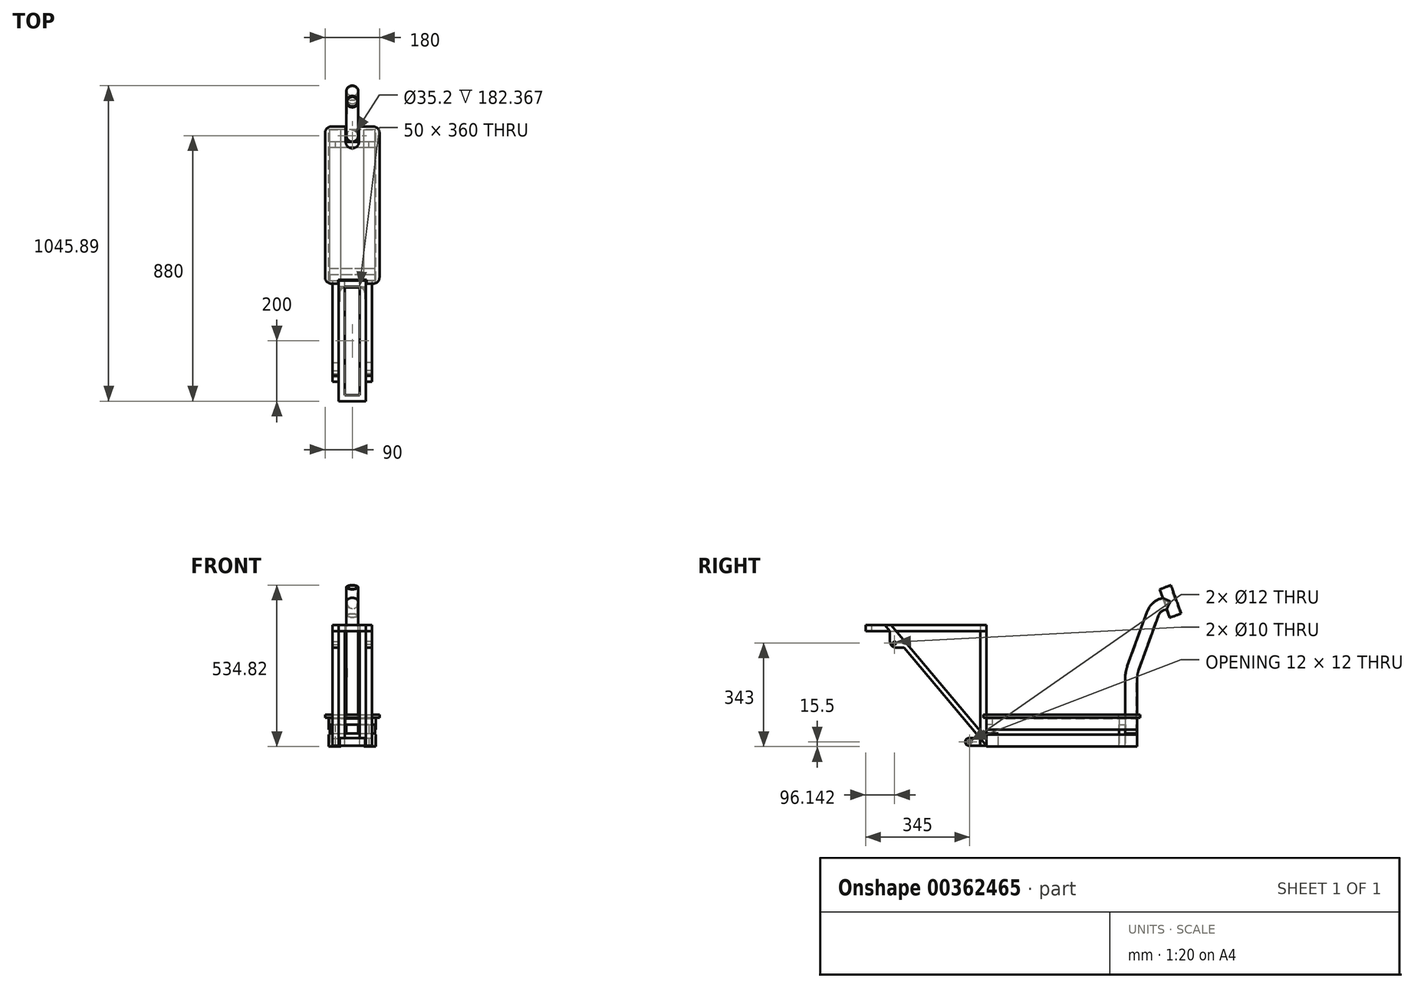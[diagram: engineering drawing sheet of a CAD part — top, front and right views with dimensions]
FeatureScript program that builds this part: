
annotation { "Feature Type Name" : "Feature", "Feature Type Description" : "" }
export const myFeature = defineFeature(function(context is Context, id is Id, definition is map)
    precondition{}
    {
        {
            var Q0;
            Q0=qCreatedBy(makeId("Front.planeOp"),FACE);
            var sketch = newSketch(context, id + "F0", { "sketchPlane" : qUnion([Q0])});
            skLineSegment(sketch, "E0.bottom", {"start": v(75, 45) * mm, "end": v(-75, 45) * mm, "construction": true});
            skLineSegment(sketch, "E0.top", {"start": v(75, -45) * mm, "end": v(-75, -45) * mm, "construction": true});
            skLineSegment(sketch, "E0.left", {"start": v(75, 45) * mm, "end": v(75, -45) * mm, "construction": true});
            skLineSegment(sketch, "E0.right", {"start": v(-75, 45) * mm, "end": v(-75, -45) * mm, "construction": true});
            skPoint(sketch, "E0.middle", {"position": v(0, 0) * mm});
            skLineSegment(sketch, "E1", {"start": v(-75, 45) * mm, "end": v(-75, 8) * mm});
            skLineSegment(sketch, "E2", {"start": v(-75, 8) * mm, "end": v(-78, 8) * mm});
            skLineSegment(sketch, "E3", {"start": v(-78, 8) * mm, "end": v(-78, 48) * mm});
            skLineSegment(sketch, "E4", {"start": v(-78, 48) * mm, "end": v(-38, 48) * mm});
            skLineSegment(sketch, "E5", {"start": v(-38, 48) * mm, "end": v(-38, 45) * mm});
            skLineSegment(sketch, "E6", {"start": v(-38, 45) * mm, "end": v(-75, 45) * mm});
            skLineSegment(sketch, "E7.MirrorCS", {"start": v(78, 48) * mm, "end": v(38, 48) * mm});
            skLineSegment(sketch, "E8.MirrorCS", {"start": v(38, 45) * mm, "end": v(75, 45) * mm});
            skLineSegment(sketch, "E9.MirrorCS", {"start": v(78, 8) * mm, "end": v(78, 48) * mm});
            skLineSegment(sketch, "E10.MirrorCS", {"start": v(75, 45) * mm, "end": v(75, 8) * mm});
            skLineSegment(sketch, "E11.MirrorCS", {"start": v(75, 8) * mm, "end": v(78, 8) * mm});
            skLineSegment(sketch, "E12.MirrorCS", {"start": v(38, 48) * mm, "end": v(38, 45) * mm});
            skLineSegment(sketch, "E13.MirrorCS", {"start": v(38, -48) * mm, "end": v(38, -45) * mm});
            skLineSegment(sketch, "E14.MirrorCS", {"start": v(75, -8) * mm, "end": v(78, -8) * mm});
            skLineSegment(sketch, "E15.MirrorCS", {"start": v(-38, -48) * mm, "end": v(-38, -45) * mm});
            skLineSegment(sketch, "E16.MirrorCS", {"start": v(-75, -8) * mm, "end": v(-78, -8) * mm});
            skLineSegment(sketch, "E17.MirrorCS", {"start": v(75, -45) * mm, "end": v(75, -8) * mm});
            skLineSegment(sketch, "E18.MirrorCS", {"start": v(78, -8) * mm, "end": v(78, -48) * mm});
            skLineSegment(sketch, "E19.MirrorCS", {"start": v(38, -45) * mm, "end": v(75, -45) * mm});
            skLineSegment(sketch, "E20.MirrorCS", {"start": v(78, -48) * mm, "end": v(38, -48) * mm});
            skLineSegment(sketch, "E21.MirrorCS", {"start": v(-38, -45) * mm, "end": v(-75, -45) * mm});
            skLineSegment(sketch, "E22.MirrorCS", {"start": v(-78, -8) * mm, "end": v(-78, -48) * mm});
            skLineSegment(sketch, "E23.MirrorCS", {"start": v(-75, -45) * mm, "end": v(-75, -8) * mm});
            skLineSegment(sketch, "E24.MirrorCS", {"start": v(-78, -48) * mm, "end": v(-38, -48) * mm});
            skLineSegment(sketch, "E25.MirrorCS", {"start": v(75, -45) * mm, "end": v(75, 45) * mm, "construction": true});
            skLineSegment(sketch, "E26.MirrorCS", {"start": v(-75, -45) * mm, "end": v(-75, 45) * mm, "construction": true});
            skSolve(sketch);
        }
        {
            var Q0;
            Q0=makeQuery(id+"F0.imprint","IMPRINT",FACE,{"disambiguationData":[TD([[makeQuery(id+"F0.imprint","IMPRINT",EDGE,{"derivedFrom":sQuery(id+"F0.wireOp",EDGE,"E1")}),-1.0]])]});
            var Q1;
            Q1=makeQuery(id+"F0.imprint","IMPRINT",FACE,{"disambiguationData":[TD([[makeQuery(id+"F0.imprint","IMPRINT",EDGE,{"derivedFrom":sQuery(id+"F0.wireOp",EDGE,"E7.MirrorCS")}),1.0]])]});
            extrude(context, id + "F1", {"entities" : qUnion([Q0, Q1]), "depth" : 500 * mm, "offsetDistance" : 25 * mm});
        }
        {
            var Q0;
            Q0=makeQuery(id+"F0.imprint","IMPRINT",FACE,{"disambiguationData":[TD([[makeQuery(id+"F0.imprint","IMPRINT",EDGE,{"derivedFrom":sQuery(id+"F0.wireOp",EDGE,"E15.MirrorCS")}),1.0]])]});
            var Q1;
            Q1=makeQuery(id+"F0.imprint","IMPRINT",FACE,{"disambiguationData":[TD([[makeQuery(id+"F0.imprint","IMPRINT",EDGE,{"derivedFrom":sQuery(id+"F0.wireOp",EDGE,"E13.MirrorCS")}),-1.0]])]});
            extrude(context, id + "F2", {"entities" : qUnion([Q0, Q1]), "depth" : 500 * mm, "offsetDistance" : 25 * mm});
        }
        {
            var Q0;
            Q0=qCreatedBy(makeId("Front.planeOp"),FACE);
            var sketch = newSketch(context, id + "F3", { "sketchPlane" : qUnion([Q0])});
            skLineSegment(sketch, "E27.top", {"start": v(75, -45) * mm, "end": v(-75, -45) * mm});
            skLineSegment(sketch, "E27.left", {"start": v(75, -5) * mm, "end": v(75, -45) * mm});
            skLineSegment(sketch, "E27.right", {"start": v(-75, -5) * mm, "end": v(-75, -45) * mm});
            skLineSegment(sketch, "E28", {"start": v(75, -5) * mm, "end": v(-75, -5) * mm});
            skSolve(sketch);
        }
        {
            var Q0;
            Q0 = qSketchRegion(id + "F3", true);
            extrude(context, id + "F4", {"entities" : qUnion([Q0]), "depth" : 40 * mm, "offsetDistance" : 25 * mm});
        }
        {
            var Q0;
            Q0=makeQuery(id+"F4.opExtrude","CAP_FACE",FACE,{"disambiguationData":[OSD([sQuery(id+"F3.wireOp",EDGE,"E27.top"),sQuery(id+"F3.wireOp",EDGE,"E27.left"),sQuery(id+"F3.wireOp",EDGE,"E27.right"),sQuery(id+"F3.wireOp",EDGE,"E28")])],"isStart":false});
            var sketch = newSketch(context, id + "F5", { "sketchPlane" : qUnion([Q0])});
            skLineSegment(sketch, "E29.0", {"start": v(75, 45) * mm, "end": v(-75, 45) * mm});
            skLineSegment(sketch, "E29.1", {"start": v(75, 45) * mm, "end": v(75, -45) * mm});
            skLineSegment(sketch, "E29.2", {"start": v(-75, -45) * mm, "end": v(-75, 45) * mm});
            skLineSegment(sketch, "E30.0", {"start": v(55, 25) * mm, "end": v(55, -45) * mm});
            skLineSegment(sketch, "E30.1", {"start": v(55, 25) * mm, "end": v(-55, 25) * mm});
            skLineSegment(sketch, "E30.2", {"start": v(-55, -45) * mm, "end": v(-55, 25) * mm});
            skLineSegment(sketch, "E31", {"start": v(75, -45) * mm, "end": v(55, -45) * mm});
            skLineSegment(sketch, "E32", {"start": v(-55, -45) * mm, "end": v(-75, -45) * mm});
            skSolve(sketch);
        }
        {
            var Q0;
            Q0 = qSketchRegion(id + "F5", true);
            extrude(context, id + "F6", {"entities" : qUnion([Q0]), "depth" : 20 * mm, "offsetDistance" : 25 * mm});
        }
        {
            var Q0;
            Q0=qCreatedBy(makeId("Front.planeOp"),FACE);
            cPlane(context, id + "F7", {"entities" : qUnion([Q0]), "cplaneType" : CPlaneType.OFFSET, "offset" : 500 * mm, "width" : 150 * mm, "height" : 150 * mm});
        }
        {
            var Q0;
            Q0=qCreatedBy(id+"F7.planeOp",FACE);
            var sketch = newSketch(context, id + "F8", { "sketchPlane" : qUnion([Q0])});
            skLineSegment(sketch, "E33.bottom", {"start": v(-75, -45) * mm, "end": v(75, -45) * mm});
            skLineSegment(sketch, "E33.top", {"start": v(-75, -5) * mm, "end": v(75, -5) * mm});
            skLineSegment(sketch, "E33.left", {"start": v(-75, -45) * mm, "end": v(-75, -5) * mm});
            skLineSegment(sketch, "E33.right", {"start": v(75, -45) * mm, "end": v(75, -5) * mm});
            skLineSegment(sketch, "E34.bottom", {"start": v(-75, 45) * mm, "end": v(75, 45) * mm});
            skLineSegment(sketch, "E34.top", {"start": v(-75, 25) * mm, "end": v(75, 25) * mm});
            skLineSegment(sketch, "E34.left", {"start": v(-75, 45) * mm, "end": v(-75, 25) * mm});
            skLineSegment(sketch, "E34.right", {"start": v(75, 45) * mm, "end": v(75, 25) * mm});
            skSolve(sketch);
        }
        {
            var Q0;
            Q0=makeQuery(id+"F8.imprint","IMPRINT",FACE,{"disambiguationData":[TD([[makeQuery(id+"F8.imprint","IMPRINT",EDGE,{"derivedFrom":sQuery(id+"F8.wireOp",EDGE,"E34.bottom")}),-1.0]])]});
            extrude(context, id + "F9", {"entities" : qUnion([Q0]), "oppositeDirection" : true, "depth" : 20 * mm, "offsetDistance" : 25 * mm});
        }
        {
            var Q0;
            Q0=makeQuery(id+"F8.imprint","IMPRINT",FACE,{"disambiguationData":[TD([[makeQuery(id+"F8.imprint","IMPRINT",EDGE,{"derivedFrom":sQuery(id+"F8.wireOp",EDGE,"E33.bottom")}),1.0]])]});
            extrude(context, id + "F10", {"entities" : qUnion([Q0]), "oppositeDirection" : true, "depth" : 40 * mm, "offsetDistance" : 25 * mm});
        }
        {
            var Q0;
            Q0=qCreatedBy(id+"F7.planeOp",FACE);
            var sketch = newSketch(context, id + "F11", { "sketchPlane" : qUnion([Q0])});
            skLineSegment(sketch, "E35.bottom", {"start": v(-25, -45) * mm, "end": v(-45, -45) * mm});
            skLineSegment(sketch, "E35.top", {"start": v(-25, 335) * mm, "end": v(-45, 335) * mm});
            skLineSegment(sketch, "E35.left", {"start": v(-25, -45) * mm, "end": v(-25, 335) * mm});
            skLineSegment(sketch, "E35.right", {"start": v(-45, -45) * mm, "end": v(-45, 335) * mm});
            skLineSegment(sketch, "E36.MirrorCS", {"start": v(25, -45) * mm, "end": v(45, -45) * mm});
            skLineSegment(sketch, "E37.MirrorCS", {"start": v(25, 335) * mm, "end": v(45, 335) * mm});
            skLineSegment(sketch, "E38.MirrorCS", {"start": v(25, -45) * mm, "end": v(25, 335) * mm});
            skLineSegment(sketch, "E39.MirrorCS", {"start": v(45, -45) * mm, "end": v(45, 335) * mm});
            skSolve(sketch);
        }
        {
            var Q0;
            Q0 = qSketchRegion(id + "F11", true);
            extrude(context, id + "F12", {"entities" : qUnion([Q0]), "operationType" : NewBodyOperationType.ADD, "depth" : 20 * mm, "offsetDistance" : 25 * mm});
        }
        {
            var Q0;
            Q0=makeQuery(id+"F12.opExtrude","SWEPT_FACE",FACE,{"disambiguationData":[OSD([sQuery(id+"F11.wireOp",EDGE,"E37.MirrorCS")])]});
            var sketch = newSketch(context, id + "F13", { "sketchPlane" : qUnion([Q0])});
            skLineSegment(sketch, "E40.bottom", {"start": v(45, -500) * mm, "end": v(-45, -500) * mm});
            skLineSegment(sketch, "E40.top", {"start": v(45, -900) * mm, "end": v(-45, -900) * mm});
            skLineSegment(sketch, "E40.left", {"start": v(45, -500) * mm, "end": v(45, -900) * mm});
            skLineSegment(sketch, "E40.right", {"start": v(-45, -500) * mm, "end": v(-45, -900) * mm});
            skLineSegment(sketch, "E41.0", {"start": v(-25, -520) * mm, "end": v(-25, -880) * mm});
            skLineSegment(sketch, "E41.1", {"start": v(25, -520) * mm, "end": v(-25, -520) * mm});
            skLineSegment(sketch, "E41.2", {"start": v(25, -520) * mm, "end": v(25, -880) * mm});
            skLineSegment(sketch, "E41.3", {"start": v(25, -880) * mm, "end": v(-25, -880) * mm});
            skSolve(sketch);
        }
        {
            var Q0;
            Q0 = qSketchRegion(id + "F13", true);
            extrude(context, id + "F14", {"entities" : qUnion([Q0]), "depth" : 20 * mm, "offsetDistance" : 25 * mm});
        }
        {
            var Q0;
            Q0=makeQuery(id+"F12.opExtrude","SWEPT_FACE",FACE,{"disambiguationData":[OSD([sQuery(id+"F11.wireOp",EDGE,"E35.right")])]});
            var sketch = newSketch(context, id + "F15", { "sketchPlane" : qUnion([Q0])});
            skLineSegment(sketch, "E42", {"start": v(500, -21.16) * mm, "end": v(815.64, 355) * mm});
            skLineSegment(sketch, "E43", {"start": v(500, -45) * mm, "end": v(772.7, 280) * mm});
            skLineSegment(sketch, "E44", {"start": v(835.64, 355) * mm, "end": v(815.64, 355) * mm});
            skLineSegment(sketch, "E45", {"start": v(500, -45) * mm, "end": v(500, -21.16) * mm});
            skLineSegment(sketch, "E46", {"start": v(818.86, 335) * mm, "end": v(818.86, 300) * mm});
            skLineSegment(sketch, "E47", {"start": v(798.86, 280) * mm, "end": v(772.7, 280) * mm});
            skCircle(sketch, "E48", {"center": v(803.86, 295) * mm, "radius": 5 * mm});
            skPoint(sketch, "E49.visualSharp", {"position": v(818.86, 280) * mm});
            skArc(sketch, "E49.filletArc", {"start": v(798.86, 280) * mm, "mid": v(813, 285.86) * mm, "end": v(818.86, 300) * mm});
            skLineSegment(sketch, "E50.trimOffspring", {"start": v(818.86, 335) * mm, "end": v(835.64, 355) * mm});
            skSolve(sketch);
        }
        {
            var Q0;
            Q0 = qSketchRegion(id + "F15", true);
            extrude(context, id + "F16", {"entities" : qUnion([Q0]), "depth" : 20 * mm, "offsetDistance" : 25 * mm});
        }
        {
            var Q0;
            Q0=makeQuery(id+"F16.opExtrude","SWEPT_BODY",BODY,{"disambiguationData":[OSD([sQuery(id+"F15.wireOp",EDGE,"E42"),sQuery(id+"F15.wireOp",EDGE,"E43"),sQuery(id+"F15.wireOp",EDGE,"E44"),sQuery(id+"F15.wireOp",EDGE,"E45")])]});
            var Q1;
            Q1=qCreatedBy(makeId("Right.planeOp"),FACE);
            mirror(context, id + "F17", {"entities" : qUnion([Q0]), "mirrorPlane" : qUnion([Q1])});
        }
        {
            var Q0;
            Q0=qCreatedBy(makeId("Right.planeOp"),FACE);
            var sketch = newSketch(context, id + "F18", { "sketchPlane" : qUnion([Q0])});
            skPoint(sketch, "E51.0", {"position": v(-20, -5) * mm});
            skLineSegment(sketch, "E52", {"start": v(-20, -5) * mm, "end": v(-20, 177.37) * mm});
            skLineSegment(sketch, "E53", {"start": v(-13.97, 211.57) * mm, "end": v(52.03, 392.89) * mm});
            skLineSegment(sketch, "E54", {"start": v(81.9, 422.77) * mm, "end": v(110, 433) * mm});
            skPoint(sketch, "E55.visualSharp", {"position": v(60, 414.8) * mm});
            skArc(sketch, "E55.filletArc", {"start": v(81.9, 422.77) * mm, "mid": v(63.65, 411.14) * mm, "end": v(52.03, 392.89) * mm});
            skPoint(sketch, "E56.visualSharp", {"position": v(-20, 195) * mm});
            skArc(sketch, "E56.filletArc", {"start": v(-13.97, 211.57) * mm, "mid": v(-18.48, 194.73) * mm, "end": v(-20, 177.37) * mm});
            skSolve(sketch);
        }
        {
            var Q0;
            Q0=makeQuery(id+"F4.opExtrude","SWEPT_EDGE",EDGE,{"disambiguationData":[OSD([sQuery(id+"F3.wireOp",EDGE,"E27.right"),sQuery(id+"F3.wireOp",EDGE,"E28")])]});
            cPoint(context, id + "F19", {"entities" : qUnion([Q0]), "parameter" : 0.5});
        }
        {
            var Q0;
            Q0 = qCreatedBy(id + "F19" ,VERTEX);
            var Q1;
            Q1=sQuery(id+"F18.wireOp",EDGE,"E52");
            cPlane(context, id + "F20", {"entities" : qUnion([Q0, Q1]), "cplaneType" : CPlaneType.LINE_POINT, "offset" : 25 * mm, "width" : 150 * mm, "height" : 150 * mm});
        }
        {
            var Q0;
            Q0=qCreatedBy(id+"F20.planeOp",FACE);
            var sketch = newSketch(context, id + "F21", { "sketchPlane" : qUnion([Q0])});
            skPoint(sketch, "E57.0", {"position": v(0, -20) * mm});
            skCircle(sketch, "E58", {"center": v(0, -20) * mm, "radius": 20 * mm});
            skCircle(sketch, "E59.0", {"center": v(0, -20) * mm, "radius": 17.6 * mm});
            skSolve(sketch);
        }
        {
            var Q0;
            Q0=makeQuery(id+"F21.imprint","IMPRINT",FACE,{"disambiguationData":[TD([[makeQuery(id+"F21.imprint","IMPRINT",EDGE,{"derivedFrom":sQuery(id+"F21.wireOp",EDGE,"E58")}),1.0]])]});
            var Q1;
            Q1=sQuery(id+"F18.wireOp",EDGE,"E53");
            var Q2;
            Q2=sQuery(id+"F18.wireOp",EDGE,"E52");
            var Q3;
            Q3=sQuery(id+"F18.wireOp",EDGE,"E56.filletArc");
            var Q4;
            Q4=sQuery(id+"F18.wireOp",EDGE,"E55.filletArc");
            var Q5;
            Q5=sQuery(id+"F18.wireOp",EDGE,"E54");
            sweep(context, id + "F22", {"profiles" : qUnion([Q0]), "path" : qUnion([Q1, Q2, Q3, Q4, Q5])});
        }
        {
            var Q0;
            Q0=makeQuery(id+"F22.opSweep","CAP_FACE",FACE,{"disambiguationData":[OSD([sQuery(id+"F18.wireOp",VERTEX,"E54.end"),sQuery(id+"F21.wireOp",EDGE,"E58"),sQuery(id+"F21.wireOp",EDGE,"E59.0")])],"isStart":false});
            var sketch = newSketch(context, id + "F23", { "sketchPlane" : qUnion([Q0])});
            skCircle(sketch, "E60.0", {"center": v(0, 369.26) * mm, "radius": 20 * mm, "construction": true});
            skLineSegment(sketch, "E61", {"start": v(0, 319.26) * mm, "end": v(0, 419.26) * mm, "construction": true});
            skLineSegment(sketch, "E62.bottom", {"start": v(0, 319.26) * mm, "end": v(-20, 319.26) * mm});
            skLineSegment(sketch, "E62.top", {"start": v(0, 419.26) * mm, "end": v(-20, 419.26) * mm});
            skLineSegment(sketch, "E62.left", {"start": v(0, 319.26) * mm, "end": v(0, 419.26) * mm});
            skLineSegment(sketch, "E62.right", {"start": v(-20, 319.26) * mm, "end": v(-20, 419.26) * mm});
            skSolve(sketch);
        }
        {
            var Q0;
            Q0=sQuery(id+"F23.wireOp",EDGE,"E61");
            var Q1;
            Q1=sQuery(id+"F23.wireOp",VERTEX,"E61.end");
            cPlane(context, id + "F24", {"entities" : qUnion([Q0, Q1]), "cplaneType" : CPlaneType.LINE_POINT, "offset" : 25 * mm, "width" : 150 * mm, "height" : 150 * mm});
        }
        {
            var Q0;
            Q0=qCreatedBy(id+"F24.planeOp",FACE);
            var sketch = newSketch(context, id + "F25", { "sketchPlane" : qUnion([Q0])});
            skCircle(sketch, "E63", {"center": v(0, 251.46) * mm, "radius": 17 * mm});
            skSolve(sketch);
        }
        {
            var Q0;
            Q0 = qSketchRegion(id + "F23", true);
            var Q1;
            Q1=sQuery(id+"F23.wireOp",EDGE,"E62.left");
            revolve(context, id + "F26", {"operationType" : NewBodyOperationType.ADD, "entities" : qUnion([Q0]), "axis" : qUnion([Q1]), "revolveType" : RevolveType.FULL});
        }
        {
            var Q0;
            Q0 = qSketchRegion(id + "F25", true);
            extrude(context, id + "F27", {"entities" : qUnion([Q0]), "operationType" : NewBodyOperationType.REMOVE, "endBound" : BoundingType.THROUGH_ALL, "oppositeDirection" : true, "depth" : 25 * mm, "offsetDistance" : 25 * mm});
        }
        {
            var Q0;
            Q0=makeQuery(id+"F1.opExtrude","SWEPT_FACE",FACE,{"disambiguationData":[OSD([sQuery(id+"F0.wireOp",EDGE,"E4")])]});
            var sketch = newSketch(context, id + "F28", { "sketchPlane" : qUnion([Q0])});
            skLineSegment(sketch, "E64.bottom", {"start": v(-70, 10) * mm, "end": v(-22, 10) * mm});
            skLineSegment(sketch, "E64.top", {"start": v(-70, -510) * mm, "end": v(-47, -510) * mm});
            skLineSegment(sketch, "E64.left", {"start": v(-90, -10) * mm, "end": v(-90, -490) * mm});
            skLineSegment(sketch, "E64.right", {"start": v(90, -10) * mm, "end": v(90, -490) * mm});
            skPoint(sketch, "E64.middle", {"position": v(0, -250) * mm});
            skPoint(sketch, "E65.visualSharp", {"position": v(-90, 10) * mm});
            skArc(sketch, "E65.filletArc", {"start": v(-70, 10) * mm, "mid": v(-84.14, 4.14) * mm, "end": v(-90, -10) * mm});
            skPoint(sketch, "E66.visualSharp", {"position": v(90, 10) * mm});
            skArc(sketch, "E66.filletArc", {"start": v(90, -10) * mm, "mid": v(84.14, 4.14) * mm, "end": v(70, 10) * mm});
            skPoint(sketch, "E67.visualSharp", {"position": v(90, -510) * mm});
            skArc(sketch, "E67.filletArc", {"start": v(70, -510) * mm, "mid": v(84.14, -504.14) * mm, "end": v(90, -490) * mm});
            skPoint(sketch, "E68.visualSharp", {"position": v(-90, -510) * mm});
            skArc(sketch, "E68.filletArc", {"start": v(-90, -490) * mm, "mid": v(-84.14, -504.14) * mm, "end": v(-70, -510) * mm});
            skArc(sketch, "E69", {"start": v(-22, -40) * mm, "mid": v(0, -62) * mm, "end": v(22, -40) * mm});
            skLineSegment(sketch, "E70", {"start": v(-22, 10) * mm, "end": v(-22, -40) * mm});
            skLineSegment(sketch, "E71", {"start": v(22, -40) * mm, "end": v(22, 10) * mm});
            skLineSegment(sketch, "E72.trimOffspring", {"start": v(22, 10) * mm, "end": v(70, 10) * mm});
            skLineSegment(sketch, "E73", {"start": v(-47, -510) * mm, "end": v(-47, -498) * mm});
            skLineSegment(sketch, "E74", {"start": v(-47, -498) * mm, "end": v(47, -498) * mm});
            skLineSegment(sketch, "E75", {"start": v(47, -498) * mm, "end": v(47, -510) * mm});
            skLineSegment(sketch, "E76.trimOffspring", {"start": v(47, -510) * mm, "end": v(70, -510) * mm});
            skSolve(sketch);
        }
        {
            var Q0;
            Q0 = qSketchRegion(id + "F28", true);
            extrude(context, id + "F29", {"entities" : qUnion([Q0]), "depth" : 10 * mm, "offsetDistance" : 25 * mm});
        }
        {
            var Q0;
            Q0=makeQuery(id+"F12.boolean.opBoolean","MERGE",FACE,{"derivedFrom":[makeQuery(id+"F10.opExtrude","SWEPT_FACE",FACE,{"disambiguationData":[OSD([sQuery(id+"F8.wireOp",EDGE,"E33.bottom")])]}),makeQuery(id+"F12.opExtrude","SWEPT_FACE",FACE,{"disambiguationData":[OSD([sQuery(id+"F11.wireOp",EDGE,"E35.bottom")])]}),makeQuery(id+"F12.opExtrude","SWEPT_FACE",FACE,{"disambiguationData":[OSD([sQuery(id+"F11.wireOp",EDGE,"E36.MirrorCS")])]})]});
            var sketch = newSketch(context, id + "F30", { "sketchPlane" : qUnion([Q0])});
            skLineSegment(sketch, "E77", {"start": v(-25, 520) * mm, "end": v(25, 520) * mm});
            skLineSegment(sketch, "E78", {"start": v(45, 540) * mm, "end": v(45, 570) * mm});
            skLineSegment(sketch, "E79", {"start": v(45, 570) * mm, "end": v(42, 570) * mm});
            skLineSegment(sketch, "E80", {"start": v(42, 570) * mm, "end": v(42, 543) * mm});
            skLineSegment(sketch, "E81", {"start": v(22, 523) * mm, "end": v(-22, 523) * mm});
            skLineSegment(sketch, "E82", {"start": v(-42, 543) * mm, "end": v(-42, 570) * mm});
            skLineSegment(sketch, "E83", {"start": v(-42, 570) * mm, "end": v(-45, 570) * mm});
            skLineSegment(sketch, "E84", {"start": v(-45, 570) * mm, "end": v(-45, 540) * mm});
            skPoint(sketch, "E85.visualSharp", {"position": v(-42, 523) * mm});
            skArc(sketch, "E85.filletArc", {"start": v(-42, 543) * mm, "mid": v(-36.14, 528.86) * mm, "end": v(-22, 523) * mm});
            skPoint(sketch, "E86.visualSharp", {"position": v(42, 523) * mm});
            skArc(sketch, "E86.filletArc", {"start": v(22, 523) * mm, "mid": v(36.14, 528.86) * mm, "end": v(42, 543) * mm});
            skPoint(sketch, "E87.visualSharp", {"position": v(-45, 520) * mm});
            skArc(sketch, "E87.filletArc", {"start": v(-45, 540) * mm, "mid": v(-39.14, 525.86) * mm, "end": v(-25, 520) * mm});
            skPoint(sketch, "E88.visualSharp", {"position": v(45, 520) * mm});
            skArc(sketch, "E88.filletArc", {"start": v(25, 520) * mm, "mid": v(39.14, 525.86) * mm, "end": v(45, 540) * mm});
            skSolve(sketch);
        }
        {
            var Q0;
            Q0 = qSketchRegion(id + "F30", true);
            extrude(context, id + "F31", {"entities" : qUnion([Q0]), "oppositeDirection" : true, "depth" : 25 * mm, "offsetDistance" : 25 * mm});
        }
        {
            var Q0;
            Q0=makeQuery(id+"F31.opExtrude","CAP_EDGE",EDGE,{"disambiguationData":[OSD([sQuery(id+"F30.wireOp",EDGE,"E83")])],"isStart":false});
            var Q1;
            Q1=makeQuery(id+"F31.opExtrude","CAP_EDGE",EDGE,{"disambiguationData":[OSD([sQuery(id+"F30.wireOp",EDGE,"E79")])],"isStart":false});
            var Q2;
            Q2=makeQuery(id+"F31.opExtrude","CAP_EDGE",EDGE,{"disambiguationData":[OSD([sQuery(id+"F30.wireOp",EDGE,"E79")])],"isStart":true});
            var Q3;
            Q3=makeQuery(id+"F31.opExtrude","CAP_EDGE",EDGE,{"disambiguationData":[OSD([sQuery(id+"F30.wireOp",EDGE,"E83")])],"isStart":true});
            fillet(context, id + "F32", {"entities" : qUnion([Q0, Q1, Q2, Q3]), "radius" : 12.5 * mm, "tangentPropagation" : true, "allowEdgeOverflow" : false});
        }
        {
            var Q0;
            Q0=makeQuery(id+"F31.opExtrude","SWEPT_FACE",FACE,{"disambiguationData":[OSD([sQuery(id+"F30.wireOp",EDGE,"E84")])]});
            var sketch = newSketch(context, id + "F33", { "sketchPlane" : qUnion([Q0])});
            skCircle(sketch, "E89", {"center": v(555, -32.5) * mm, "radius": 6 * mm});
            skSolve(sketch);
        }
        {
            var Q0;
            Q0 = qSketchRegion(id + "F33", true);
            extrude(context, id + "F34", {"entities" : qUnion([Q0]), "operationType" : NewBodyOperationType.REMOVE, "endBound" : BoundingType.THROUGH_ALL, "oppositeDirection" : true, "depth" : 25 * mm, "offsetDistance" : 25 * mm});
        }
    });
